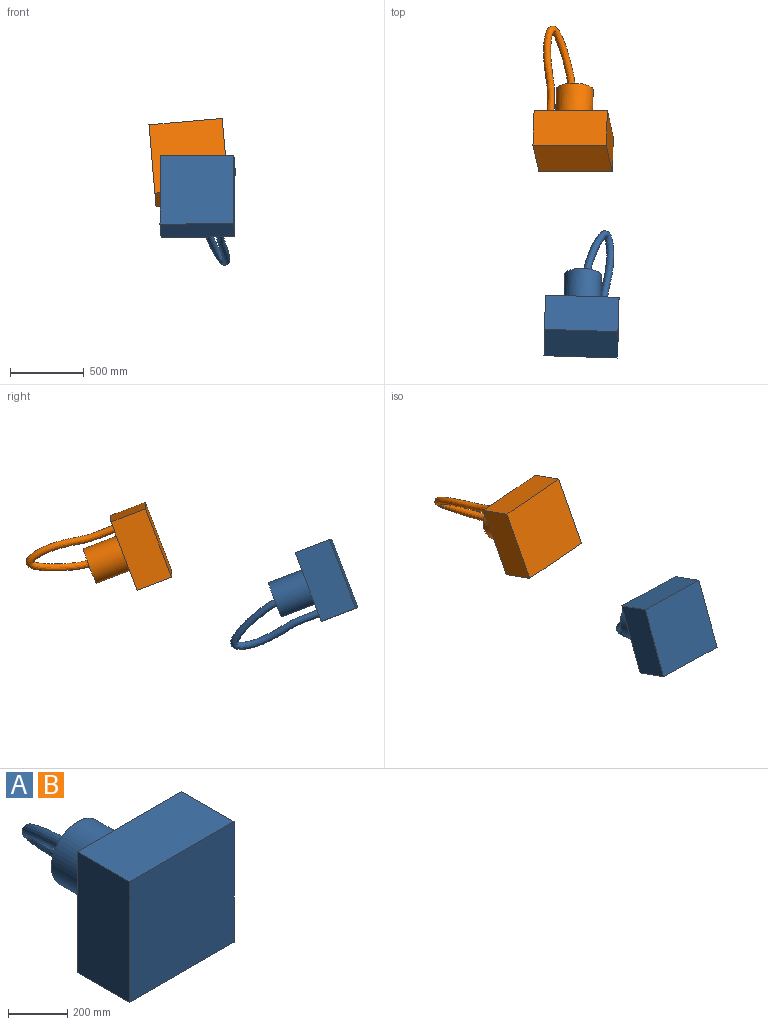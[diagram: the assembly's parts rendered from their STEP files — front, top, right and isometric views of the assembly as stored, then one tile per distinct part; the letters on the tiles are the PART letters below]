
ASSEMBLY  parts=2 mates=1
PART A: 10 faces, bbox 500x892.3x501.1 mm
  f0: plane 500x250mm, normal (-1,0,0), area 125000mm2, adj f2,f3,f4,f6
  f1: plane 500x250mm, normal (1,0,0), area 125000mm2, adj f2,f3,f4,f6
  f2: plane 500x500mm, normal (0,-1,0), area 250000mm2, adj f0,f1,f3,f4
  f3: plane 500x250mm, normal (0,0,1), area 125000mm2, adj f0,f1,f2,f6
  f4: plane 500x250mm, normal (0,0,-1), area 125000mm2, adj f0,f1,f2,f6
  f5: cylinder r=125mm len=250mm, axis (0,1,0), area 196349.5mm2, adj f6,f7
  f6: plane 500x500mm, normal (0,1,0), area 199018.1mm2, adj f0,f1,f3,f4,f5,f9
  f7: plane 250x250mm, normal (0,1,0), area 48139.6mm2, adj f5,f8,f9
  f8: plane 46.61x35.32mm, normal (-0.05,-1,0.02), area 947.3mm2, adj f7,f9
  f9: bspline ~642.32x254.89mm, area 166354mm2, adj f6,f7,f8
PART B: same geometry as A
PLACE A rot(axis=(-1,0,-0.09),21deg) t=(10.35,-69.91,126.83)mm
PLACE B rot(axis=(0.01,0.98,-0.18),175.1deg) t=(-46.63,1189.94,356.7)mm
MATE parallel B.f5 <-> A.f5  axis (-0.03,-0.93,0.36) through (-54.44,956.54,445.95)mm
